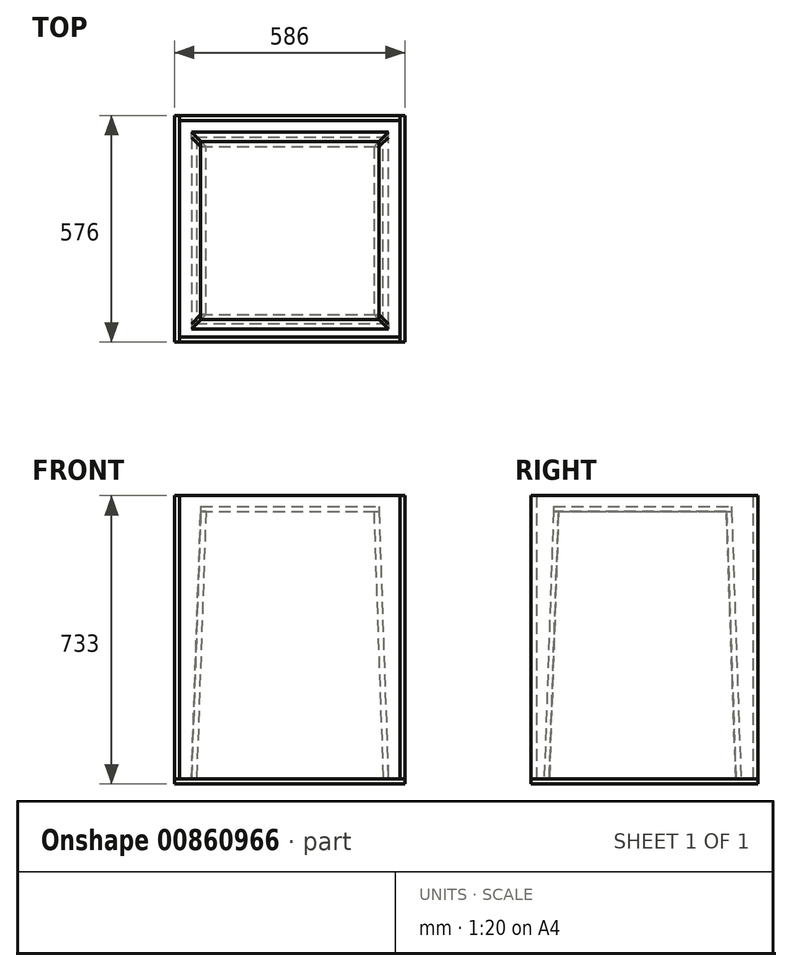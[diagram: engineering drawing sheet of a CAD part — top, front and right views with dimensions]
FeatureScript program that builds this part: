
annotation { "Feature Type Name" : "Feature", "Feature Type Description" : "" }
export const myFeature = defineFeature(function(context is Context, id is Id, definition is map)
    precondition{}
    {
        {
            var Q0;
            Q0=qCreatedBy(makeId("Top.planeOp"),FACE);
            var sketch = newSketch(context, id + "F0", { "sketchPlane" : qUnion([Q0])});
            skLineSegment(sketch, "E0.bottom", {"start": v(-250, 250) * mm, "end": v(250, 250) * mm, "construction": true});
            skLineSegment(sketch, "E0.top", {"start": v(-250, -250) * mm, "end": v(250, -250) * mm, "construction": true});
            skLineSegment(sketch, "E0.left", {"start": v(-250, 250) * mm, "end": v(-250, -250) * mm, "construction": true});
            skLineSegment(sketch, "E0.right", {"start": v(250, 250) * mm, "end": v(250, -250) * mm, "construction": true});
            skSolve(sketch);
        }
        {
            var Q0;
            Q0=sQuery(id+"F0.wireOp",EDGE,"E0.top");
            cPlane(context, id + "F1", {"entities" : qUnion([Q0]), "cplaneType" : CPlaneType.LINE_ANGLE, "offset" : 25 * mm, "angle" : 2 * degree, "oppositeDirection" : true, "width" : 150 * mm, "height" : 150 * mm});
        }
        {
            var Q0;
            Q0=sQuery(id+"F0.wireOp",EDGE,"E0.bottom");
            cPlane(context, id + "F2", {"entities" : qUnion([Q0]), "cplaneType" : CPlaneType.LINE_ANGLE, "offset" : 25 * mm, "angle" : 2 * degree, "width" : 150 * mm, "height" : 150 * mm});
        }
        {
            var Q0;
            Q0=sQuery(id+"F0.wireOp",EDGE,"E0.left");
            cPlane(context, id + "F3", {"entities" : qUnion([Q0]), "cplaneType" : CPlaneType.LINE_ANGLE, "offset" : 25 * mm, "angle" : 92 * degree, "oppositeDirection" : true, "width" : 150 * mm, "height" : 150 * mm});
        }
        {
            var Q0;
            Q0=sQuery(id+"F0.wireOp",EDGE,"E0.right");
            cPlane(context, id + "F4", {"entities" : qUnion([Q0]), "cplaneType" : CPlaneType.LINE_ANGLE, "offset" : 25 * mm, "angle" : 92 * degree, "width" : 150 * mm, "height" : 150 * mm});
        }
        {
            var Q0;
            Q0=qCreatedBy(makeId("Top.planeOp"),FACE);
            cPlane(context, id + "F5", {"entities" : qUnion([Q0]), "cplaneType" : CPlaneType.OFFSET, "offset" : 680 * mm, "width" : 150 * mm, "height" : 150 * mm});
        }
        {
            var Q0;
            Q0=qCreatedBy(id+"F1.planeOp",FACE);
            var sketch = newSketch(context, id + "F6", { "sketchPlane" : qUnion([Q0])});
            skLineSegment(sketch, "E1", {"start": v(-250, -8.72) * mm, "end": v(250, -8.72) * mm});
            skLineSegment(sketch, "E2", {"start": v(250, -8.72) * mm, "end": v(226.25, 671.69) * mm});
            skLineSegment(sketch, "E3", {"start": v(226.25, 671.69) * mm, "end": v(-226.25, 671.69) * mm});
            skLineSegment(sketch, "E4", {"start": v(-226.25, 671.69) * mm, "end": v(-250, -8.72) * mm});
            skSolve(sketch);
        }
        {
            var Q0;
            Q0=makeQuery(id+"F6.imprint","IMPRINT",FACE,{"disambiguationData":[TD([[makeQuery(id+"F6.imprint","IMPRINT",EDGE,{"derivedFrom":sQuery(id+"F6.wireOp",EDGE,"E1")}),1.0]])]});
            extrude(context, id + "F7", {"entities" : qUnion([Q0]), "depth" : 13 * mm, "offsetDistance" : 25 * mm});
        }
        {
            var Q0;
            Q0=qCreatedBy(id+"F2.planeOp",FACE);
            var sketch = newSketch(context, id + "F8", { "sketchPlane" : qUnion([Q0])});
            skLineSegment(sketch, "E5", {"start": v(-250, -8.72) * mm, "end": v(250, -8.72) * mm});
            skLineSegment(sketch, "E6", {"start": v(250, -8.72) * mm, "end": v(226.25, 671.69) * mm});
            skLineSegment(sketch, "E7", {"start": v(226.25, 671.69) * mm, "end": v(-226.25, 671.69) * mm});
            skLineSegment(sketch, "E8", {"start": v(-226.25, 671.69) * mm, "end": v(-250, -8.72) * mm});
            skSolve(sketch);
        }
        {
            var Q0;
            Q0=makeQuery(id+"F8.imprint","IMPRINT",FACE,{"disambiguationData":[TD([[makeQuery(id+"F8.imprint","IMPRINT",EDGE,{"derivedFrom":sQuery(id+"F8.wireOp",EDGE,"E5")}),1.0]])]});
            extrude(context, id + "F9", {"entities" : qUnion([Q0]), "oppositeDirection" : true, "depth" : 13 * mm, "offsetDistance" : 25 * mm});
        }
        {
            var Q0;
            Q0=qCreatedBy(id+"F3.planeOp",FACE);
            var sketch = newSketch(context, id + "F10", { "sketchPlane" : qUnion([Q0])});
            skLineSegment(sketch, "E9", {"start": v(-237, -9.18) * mm, "end": v(237, -9.18) * mm});
            skLineSegment(sketch, "E10", {"start": v(237, -9.18) * mm, "end": v(213.26, 671.24) * mm});
            skLineSegment(sketch, "E11", {"start": v(213.26, 671.24) * mm, "end": v(-213.26, 671.24) * mm});
            skLineSegment(sketch, "E12", {"start": v(-213.26, 671.24) * mm, "end": v(-237, -9.18) * mm});
            skSolve(sketch);
        }
        {
            var Q0;
            Q0 = qSketchRegion(id + "F10", true);
            extrude(context, id + "F11", {"entities" : qUnion([Q0]), "oppositeDirection" : true, "depth" : 13 * mm, "offsetDistance" : 25 * mm});
        }
        {
            var Q0;
            Q0=qCreatedBy(id+"F4.planeOp",FACE);
            var sketch = newSketch(context, id + "F12", { "sketchPlane" : qUnion([Q0])});
            skLineSegment(sketch, "E13", {"start": v(-237, -9.18) * mm, "end": v(237, -9.18) * mm});
            skLineSegment(sketch, "E14", {"start": v(237, -9.18) * mm, "end": v(213.25, 671.69) * mm});
            skLineSegment(sketch, "E15", {"start": v(213.25, 671.69) * mm, "end": v(-213.25, 671.69) * mm});
            skLineSegment(sketch, "E16", {"start": v(-213.25, 671.69) * mm, "end": v(-237, -9.18) * mm});
            skSolve(sketch);
        }
        {
            var Q0;
            Q0 = qSketchRegion(id + "F12", true);
            extrude(context, id + "F13", {"entities" : qUnion([Q0]), "oppositeDirection" : true, "depth" : 13 * mm, "offsetDistance" : 25 * mm});
        }
        {
            var Q0;
            Q0=qCreatedBy(id+"F5.planeOp",FACE);
            var sketch = newSketch(context, id + "F14", { "sketchPlane" : qUnion([Q0])});
            skLineSegment(sketch, "E17", {"start": v(226.25, -226.25) * mm, "end": v(226.25, 226.25) * mm});
            skLineSegment(sketch, "E18", {"start": v(226.25, 226.25) * mm, "end": v(-226.27, 226.25) * mm});
            skLineSegment(sketch, "E19", {"start": v(-226.27, 226.25) * mm, "end": v(-226.27, -226.25) * mm});
            skLineSegment(sketch, "E20", {"start": v(-226.27, -226.25) * mm, "end": v(226.25, -226.25) * mm});
            skSolve(sketch);
        }
        {
            var Q0;
            Q0 = qSketchRegion(id + "F14", true);
            extrude(context, id + "F15", {"entities" : qUnion([Q0]), "depth" : 13 * mm, "offsetDistance" : 25 * mm});
        }
        {
            var Q0;
            Q0=qCreatedBy(makeId("Front.planeOp"),FACE);
            cPlane(context, id + "F16", {"entities" : qUnion([Q0]), "cplaneType" : CPlaneType.OFFSET, "offset" : 270 * mm, "width" : 150 * mm, "height" : 150 * mm});
        }
        {
            var Q0;
            Q0=qCreatedBy(id+"F16.planeOp",FACE);
            var sketch = newSketch(context, id + "F17", { "sketchPlane" : qUnion([Q0])});
            skLineSegment(sketch, "E21.bottom", {"start": v(-280, 720) * mm, "end": v(280, 720) * mm});
            skLineSegment(sketch, "E21.top", {"start": v(-280, 0) * mm, "end": v(280, 0) * mm});
            skLineSegment(sketch, "E21.left", {"start": v(-280, 720) * mm, "end": v(-280, 0) * mm});
            skLineSegment(sketch, "E21.right", {"start": v(280, 720) * mm, "end": v(280, 0) * mm});
            skSolve(sketch);
        }
        {
            var Q0;
            Q0 = qSketchRegion(id + "F17", true);
            extrude(context, id + "F18", {"entities" : qUnion([Q0]), "depth" : 13 * mm, "offsetDistance" : 25 * mm});
        }
        {
            var Q0;
            Q0=qCreatedBy(makeId("Front.planeOp"),FACE);
            cPlane(context, id + "F19", {"entities" : qUnion([Q0]), "cplaneType" : CPlaneType.OFFSET, "offset" : 280 * mm, "oppositeDirection" : true, "width" : 150 * mm, "height" : 150 * mm});
        }
        {
            var Q0;
            Q0=qCreatedBy(id+"F19.planeOp",FACE);
            var sketch = newSketch(context, id + "F20", { "sketchPlane" : qUnion([Q0])});
            skLineSegment(sketch, "E22.bottom", {"start": v(280, 720) * mm, "end": v(-280, 720) * mm});
            skLineSegment(sketch, "E22.top", {"start": v(280, 0) * mm, "end": v(-280, 0) * mm});
            skLineSegment(sketch, "E22.left", {"start": v(280, 720) * mm, "end": v(280, 0) * mm});
            skLineSegment(sketch, "E22.right", {"start": v(-280, 720) * mm, "end": v(-280, 0) * mm});
            skSolve(sketch);
        }
        {
            var Q0;
            Q0 = qSketchRegion(id + "F20", true);
            extrude(context, id + "F21", {"entities" : qUnion([Q0]), "oppositeDirection" : true, "depth" : 13 * mm, "offsetDistance" : 25 * mm});
        }
        {
            var Q0;
            Q0=qCreatedBy(makeId("Right.planeOp"),FACE);
            cPlane(context, id + "F22", {"entities" : qUnion([Q0]), "cplaneType" : CPlaneType.OFFSET, "offset" : 280 * mm, "width" : 150 * mm, "height" : 150 * mm});
        }
        {
            var Q0;
            Q0=qCreatedBy(makeId("Right.planeOp"),FACE);
            cPlane(context, id + "F23", {"entities" : qUnion([Q0]), "cplaneType" : CPlaneType.OFFSET, "offset" : 280 * mm, "oppositeDirection" : true, "width" : 150 * mm, "height" : 150 * mm});
        }
        {
            var Q0;
            Q0=qCreatedBy(id+"F22.planeOp",FACE);
            var sketch = newSketch(context, id + "F24", { "sketchPlane" : qUnion([Q0])});
            skLineSegment(sketch, "E23.bottom", {"start": v(-283, 720) * mm, "end": v(293, 720) * mm});
            skLineSegment(sketch, "E23.top", {"start": v(-283, 0) * mm, "end": v(293, 0) * mm});
            skLineSegment(sketch, "E23.left", {"start": v(-283, 720) * mm, "end": v(-283, 0) * mm});
            skLineSegment(sketch, "E23.right", {"start": v(293, 720) * mm, "end": v(293, 0) * mm});
            skSolve(sketch);
        }
        {
            var Q0;
            Q0 = qSketchRegion(id + "F24", true);
            extrude(context, id + "F25", {"entities" : qUnion([Q0]), "depth" : 13 * mm, "offsetDistance" : 25 * mm});
        }
        {
            var Q0;
            Q0=qCreatedBy(id+"F23.planeOp",FACE);
            var sketch = newSketch(context, id + "F26", { "sketchPlane" : qUnion([Q0])});
            skLineSegment(sketch, "E24.bottom", {"start": v(-283, 0) * mm, "end": v(293, 0) * mm});
            skLineSegment(sketch, "E24.top", {"start": v(-283, 720) * mm, "end": v(293, 720) * mm});
            skLineSegment(sketch, "E24.left", {"start": v(-283, 0) * mm, "end": v(-283, 720) * mm});
            skLineSegment(sketch, "E24.right", {"start": v(293, 0) * mm, "end": v(293, 720) * mm});
            skSolve(sketch);
        }
        {
            var Q0;
            Q0 = qSketchRegion(id + "F26", true);
            extrude(context, id + "F27", {"entities" : qUnion([Q0]), "oppositeDirection" : true, "depth" : 13 * mm, "offsetDistance" : 25 * mm});
        }
        {
            var Q0;
            Q0=qCreatedBy(makeId("Top.planeOp"),FACE);
            var sketch = newSketch(context, id + "F28", { "sketchPlane" : qUnion([Q0])});
            skLineSegment(sketch, "E25.bottom", {"start": v(293, 293) * mm, "end": v(-293, 293) * mm});
            skLineSegment(sketch, "E25.top", {"start": v(293, -283) * mm, "end": v(-293, -283) * mm});
            skLineSegment(sketch, "E25.left", {"start": v(293, 293) * mm, "end": v(293, -283) * mm});
            skLineSegment(sketch, "E25.right", {"start": v(-293, 293) * mm, "end": v(-293, -283) * mm});
            skSolve(sketch);
        }
        {
            var Q0;
            Q0 = qSketchRegion(id + "F28", true);
            extrude(context, id + "F29", {"entities" : qUnion([Q0]), "oppositeDirection" : true, "depth" : 13 * mm, "offsetDistance" : 25 * mm});
        }
    });
